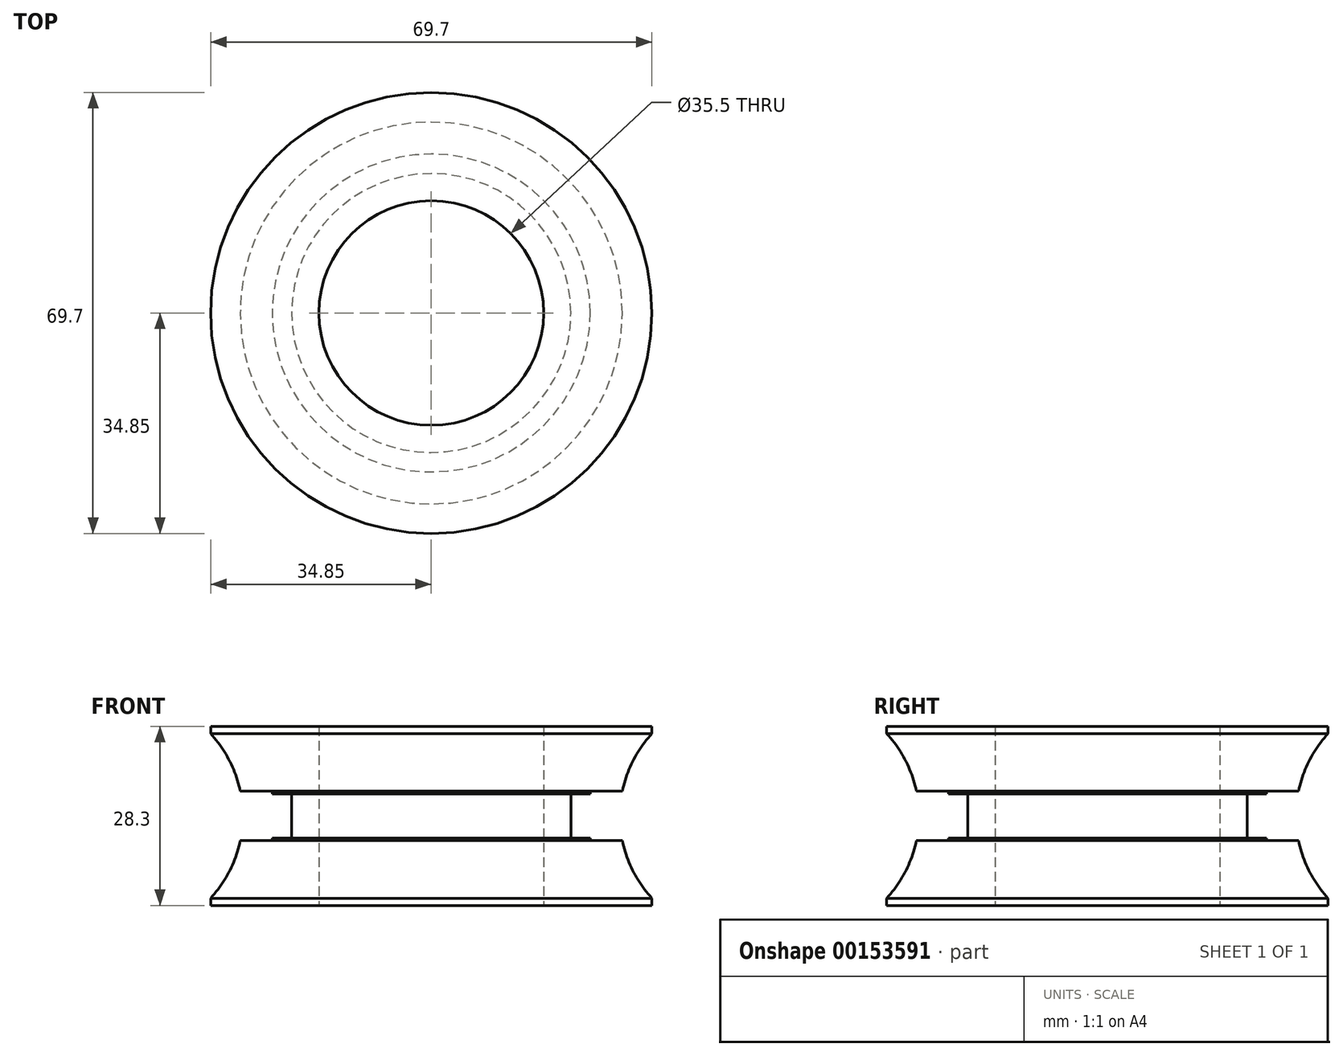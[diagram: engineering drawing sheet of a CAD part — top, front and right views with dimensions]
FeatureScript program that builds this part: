
annotation { "Feature Type Name" : "Feature", "Feature Type Description" : "" }
export const myFeature = defineFeature(function(context is Context, id is Id, definition is map)
    precondition{}
    {
        {
            var Q0;
            Q0=qCreatedBy(makeId("Front.planeOp"),FACE);
            var sketch = newSketch(context, id + "F0", { "sketchPlane" : qUnion([Q0])});
            skLineSegment(sketch, "E0", {"start": v(0, 0) * mm, "end": v(0, 28) * mm, "construction": true});
            skLineSegment(sketch, "E1", {"start": v(-17.75, -0.5) * mm, "end": v(-17.75, 13.65) * mm});
            skLineSegment(sketch, "E2", {"start": v(-36, -0.5) * mm, "end": v(-36, 27.8) * mm, "construction": true});
            skLineSegment(sketch, "E3", {"start": v(-30, 27.8) * mm, "end": v(-30, -0.5) * mm, "construction": true});
            skLineSegment(sketch, "E4", {"start": v(-22.05, 10.15) * mm, "end": v(-22.05, 17.15) * mm});
            skPoint(sketch, "E5", {"position": v(-22.05, 10.15) * mm});
            skLineSegment(sketch, "E6", {"start": v(-17.75, 0) * mm, "end": v(-25.12, 0) * mm});
            skLineSegment(sketch, "E7", {"start": v(-25.12, 17.55) * mm, "end": v(-25.12, 17.15) * mm});
            skPoint(sketch, "E8", {"position": v(-22.05, 17.15) * mm});
            skPoint(sketch, "E9.orphan", {"position": v(-22.05, 27.8) * mm});
            skPoint(sketch, "E10.orphan", {"position": v(-22.05, 0) * mm});
            skPoint(sketch, "E11", {"position": v(-25.12, 9.75) * mm});
            skPoint(sketch, "E12", {"position": v(-22.05, 13.65) * mm});
            skLineSegment(sketch, "E13", {"start": v(-22.05, 10.15) * mm, "end": v(-25.12, 10.15) * mm});
            skLineSegment(sketch, "E14", {"start": v(-25.12, 9.75) * mm, "end": v(-30.18, 9.75) * mm});
            skLineSegment(sketch, "E15", {"start": v(-36, 13.65) * mm, "end": v(0, 13.65) * mm, "construction": true});
            skLineSegment(sketch, "E16.MirrorCS", {"start": v(-22.05, 17.15) * mm, "end": v(-25.12, 17.15) * mm});
            skLineSegment(sketch, "E17.MirrorCS", {"start": v(-25.12, 17.55) * mm, "end": v(-30.18, 17.55) * mm});
            skPoint(sketch, "E18.start.orphan", {"position": v(-17.75, 27.8) * mm});
            skLineSegment(sketch, "E19.MirrorCS", {"start": v(-17.75, 27.3) * mm, "end": v(-25.12, 27.3) * mm});
            skLineSegment(sketch, "E20.MirrorCS", {"start": v(-17.75, 27.8) * mm, "end": v(-17.75, 13.65) * mm});
            skLineSegment(sketch, "E21.MirrorCS", {"start": v(-25.12, 9.75) * mm, "end": v(-25.12, 10.15) * mm});
            skLineSegment(sketch, "E22.trimOffspring", {"start": v(-25.12, 10.15) * mm, "end": v(-25.12, -0.5) * mm});
            skLineSegment(sketch, "E23.trimOffspring", {"start": v(-25.12, 17.15) * mm, "end": v(-25.12, 27.8) * mm});
            skPoint(sketch, "E24.positionSnap0", {"position": v(-35.74, 13.9) * mm});
            skCircle(sketch, "E25", {"center": v(-48.98, 13.65) * mm, "radius": 19.2 * mm});
            skLineSegment(sketch, "E26", {"start": v(-48.98, 13.65) * mm, "end": v(-29.78, 13.65) * mm, "construction": true});
            skLineSegment(sketch, "E27", {"start": v(-22.05, 13.65) * mm, "end": v(-17.75, 13.65) * mm});
            skLineSegment(sketch, "E28", {"start": v(-36, 27.8) * mm, "end": v(-17.75, 27.8) * mm});
            skLineSegment(sketch, "E29.MirrorCS", {"start": v(-36, -0.5) * mm, "end": v(-17.75, -0.5) * mm});
            skPoint(sketch, "E30.orphan", {"position": v(-25.12, 0) * mm});
            skPoint(sketch, "E31.orphan", {"position": v(-30, 0) * mm});
            skPoint(sketch, "E32.orphan", {"position": v(-25.12, 27.3) * mm});
            skPoint(sketch, "E33.orphan", {"position": v(-17.75, 27.3) * mm});
            skPoint(sketch, "E34.orphan", {"position": v(-36, 27.3) * mm});
            skPoint(sketch, "E35.trimOffspring.end.orphan", {"position": v(-36, 0) * mm});
            skLineSegment(sketch, "E36", {"start": v(-36, 13.65) * mm, "end": v(-36, 27.8) * mm});
            skLineSegment(sketch, "E37.MirrorCS", {"start": v(-36, 13.65) * mm, "end": v(-36, -0.5) * mm});
            skPoint(sketch, "E38.orphan", {"position": v(-36, 27.8) * mm});
            skPoint(sketch, "E39.end.orphan", {"position": v(-35.48, 0) * mm});
            skPoint(sketch, "E40.orphan", {"position": v(-30, 17.55) * mm});
            skPoint(sketch, "E41.orphan", {"position": v(-30, 9.75) * mm});
            skSolve(sketch);
        }
        {
            var Q0;
            {var subQ3=sQuery(id+"F0.wireOp",EDGE,"E6");Q0=makeQuery(id+"F0.imprint","IMPRINT",FACE,{"disambiguationData":[TD([[makeQuery(id+"F0.imprint","IMPRINT",EDGE,{"derivedFrom":subQ3}),1.0]])]});}
            var Q1;
            {var subQ0=sQuery(id+"F0.wireOp",EDGE,"E19.MirrorCS");Q1=makeQuery(id+"F0.imprint","IMPRINT",FACE,{"disambiguationData":[TD([[makeQuery(id+"F0.imprint","IMPRINT",EDGE,{"derivedFrom":subQ0}),-1.0]])]});}
            var Q2;
            {var subQ1=sQuery(id+"F0.wireOp",EDGE,"E6");Q2=makeQuery(id+"F0.imprint","IMPRINT",FACE,{"disambiguationData":[TD([[makeQuery(id+"F0.imprint","IMPRINT",EDGE,{"derivedFrom":subQ1}),-1.0]])]});}
            var Q3;
            {var subQ5=sQuery(id+"F0.wireOp",EDGE,"E16.MirrorCS");Q3=makeQuery(id+"F0.imprint","IMPRINT",FACE,{"disambiguationData":[TD([[makeQuery(id+"F0.imprint","IMPRINT",EDGE,{"derivedFrom":subQ5}),-1.0]])]});}
            var Q4;
            {var subQ1=sQuery(id+"F0.wireOp",EDGE,"E17.MirrorCS");Q4=makeQuery(id+"F0.imprint","IMPRINT",FACE,{"disambiguationData":[TD([[makeQuery(id+"F0.imprint","IMPRINT",EDGE,{"derivedFrom":subQ1}),-1.0]])]});}
            var Q5;
            {var subQ6=sQuery(id+"F0.wireOp",EDGE,"E14");Q5=makeQuery(id+"F0.imprint","IMPRINT",FACE,{"disambiguationData":[TD([[makeQuery(id+"F0.imprint","IMPRINT",EDGE,{"derivedFrom":subQ6}),1.0]])]});}
            var Q6;
            Q6=sQuery(id+"F0.wireOp",EDGE,"E0");
            revolve(context, id + "F1", {"entities" : qUnion([Q0, Q1, Q2, Q3, Q4, Q5]), "axis" : qUnion([Q6]), "revolveType" : RevolveType.FULL});
        }
        {
            var Q0;
            Q0=makeQuery(id+"F1.opRevolve","SWEPT_EDGE",EDGE,{"disambiguationData":[OSD([sQuery(id+"F0.wireOp",EDGE,"E25"),sQuery(id+"F0.wireOp",EDGE,"E28"),sQuery(id+"F0.wireOp",EDGE,"E36")])]});
            chamfer(context, id + "F2", {"entities" : qUnion([Q0]), "chamferType" : ChamferType.OFFSET_ANGLE, "width" : 1.25 * mm, "oppositeDirection" : true, "angle" : 90 * degree, "tangentPropagation" : true});
        }
        {
            var Q0;
            Q0=makeQuery(id+"F1.opRevolve","SWEPT_EDGE",EDGE,{"disambiguationData":[OSD([sQuery(id+"F0.wireOp",EDGE,"E6"),sQuery(id+"F0.wireOp",EDGE,"ufRsHZx0-bAzl-OTeD-VbQE-DXJWGsWiAcSt")])]});
            var Q1;
            Q1=makeQuery(id+"F1.opRevolve","SWEPT_EDGE",EDGE,{"disambiguationData":[OSD([sQuery(id+"F0.wireOp",EDGE,"E25"),sQuery(id+"F0.wireOp",EDGE,"E29.MirrorCS"),sQuery(id+"F0.wireOp",EDGE,"E37.MirrorCS")])]});
            chamfer(context, id + "F3", {"entities" : qUnion([Q0, Q1]), "chamferType" : ChamferType.OFFSET_ANGLE, "width" : 1.25 * mm, "oppositeDirection" : false, "angle" : 90 * degree, "tangentPropagation" : true});
        }
    });
